# Revit family: Seitenhalter - SH KAB 20 FS
name_source: partatom
category: Generic Models
revit_build: Autodesk Revit 2017 (Build: 20190508_0315(x64)
units: mm (PartAtom-declared; Revit-internal decimal feet)

## family parameters
Always vertical = Yes
Can host rebar = No
Cut with Voids When Loaded = No
Part Type = Normal
Room Calculation Point = No
Round Connector Dimension = Use Diameter
Shared = No
Work Plane-Based = No

## types (2) — shared parameters
Manufacturer = OBO BETTERMANN
Material = Strip-galvanised
URL = http://www.obo-bettermann.com

## per-type parameters (varying)
| type | Diameter | GTIN | Manufacturer Art.No. |
| SH KAB 20 FS | 20 mm  [stored 0.0656168 ft] | 4012196649990 | 6015425 |
| SH KAB 25 FS | 25 mm  [stored 0.082021 ft] | 4012196650057 | 6015433 |

note: column(s) folded — value = type name in every type: Article Type

note: [stored X ft] marks values corroborated as IEEE doubles in the binary element streams (Revit-internal decimal feet)

## geometry (parser evidence)
native form markers: Sweep x2
no freeform markers — native parametric forms only
